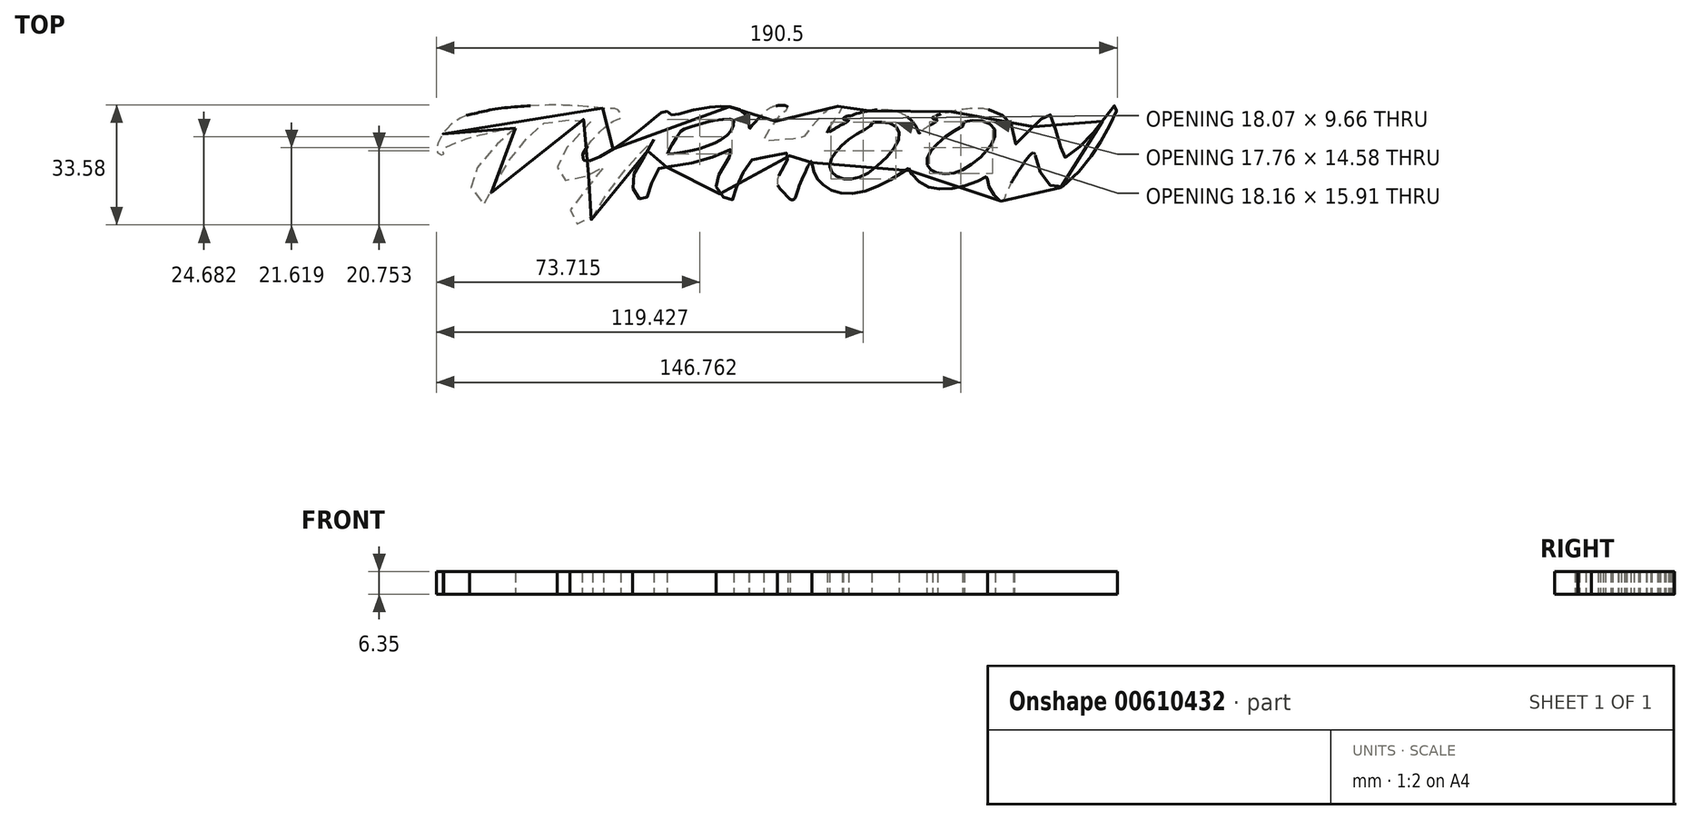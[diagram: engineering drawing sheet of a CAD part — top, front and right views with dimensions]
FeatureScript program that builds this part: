
annotation { "Feature Type Name" : "Feature", "Feature Type Description" : "" }
export const myFeature = defineFeature(function(context is Context, id is Id, definition is map)
    precondition{}
    {
        {
            var Q0;
            Q0=qCreatedBy(makeId("Top.planeOp"),FACE);
            var sketch = newSketch(context, id + "F0", { "sketchPlane" : qUnion([Q0])});
            skFitSpline(sketch, "E0", {"points": [v(22.1, 27.14) * mm, v(21.78, 26.76) * mm, v(21.16, 26.2) * mm, v(20.1, 25.33) * mm, v(18.79, 24.27) * mm, v(17.27, 22.87) * mm, v(15.75, 21.37) * mm, v(13.77, 19.23) * mm, v(12.34, 17.4) * mm, v(11.48, 16.05) * mm, v(10.24, 14.4) * mm, v(9.46, 13) * mm, v(9.33, 12.48) * mm, v(9.34, 11.55) * mm, v(9.5, 10.95) * mm, v(9.92, 10.08) * mm, v(10.5, 9) * mm, v(11.5, 7.36) * mm, v(12.18, 6.47) * mm, v(12.71, 6) * mm, v(13.12, 5.77) * mm, v(13.66, 5.75) * mm, v(14.18, 6.12) * mm, v(14.82, 7.38) * mm, v(15.18, 8.54) * mm, v(15.82, 10.13) * mm, v(16.47, 11.51) * mm, v(17.1, 12.84) * mm, v(18.08, 14.59) * mm, v(19.1, 16.22) * mm, v(20.35, 18.06) * mm, v(21.44, 19.5) * mm, v(22.74, 21.15) * mm, v(24.07, 22.8) * mm, v(25.67, 24.63) * mm, v(27.2, 26.39) * mm, v(28.29, 27.58) * mm, v(28.8, 28.03) * mm, v(29.3, 28.34) * mm, v(29.72, 28.46) * mm, v(30.82, 28.58) * mm, v(32, 28.77) * mm, v(33.32, 28.96) * mm, v(35.58, 29.2) * mm, v(37.22, 29.34) * mm, v(40.15, 29.47) * mm, v(42.2, 29.53) * mm, v(43.65, 29.52) * mm, v(43.74, 29.47) * mm, v(43.69, 29.35) * mm, v(43.37, 28.97) * mm, v(41.41, 27.03) * mm, v(39.35, 24.88) * mm, v(37.53, 22.86) * mm, v(35.8, 20.64) * mm, v(35.04, 19.48) * mm, v(34.48, 18.52) * mm, v(34.03, 17.42) * mm, v(33.9, 16.94) * mm, v(33.8, 16.2) * mm, v(33.8, 15.49) * mm, v(33.95, 14.67) * mm, v(34.14, 14.14) * mm, v(34.37, 13.75) * mm, v(34.64, 13.43) * mm, v(35.23, 12.92) * mm, v(35.95, 12.53) * mm, v(36.78, 12.28) * mm, v(37.78, 12.2) * mm, v(38.96, 12.31) * mm, v(40.2, 12.82) * mm, v(41.49, 13.43) * mm, v(42.62, 14.06) * mm, v(44.3, 15.13) * mm, v(45.26, 15.76) * mm, v(46, 16.13) * mm, v(46.39, 16.25) * mm, v(46.76, 16.25) * mm, v(46.82, 16.18) * mm, v(46.76, 15.83) * mm, v(46.5, 15.4) * mm, v(45.67, 14.52) * mm, v(44.26, 12.88) * mm, v(42.81, 11.13) * mm, v(41, 8.86) * mm, v(39.54, 6.95) * mm, v(38.25, 5.3) * mm, v(37.77, 4.7) * mm, v(37.43, 4) * mm, v(37.34, 3.46) * mm, v(37.32, 2.67) * mm, v(37.5, 2.03) * mm, v(37.99, 1.26) * mm, v(38.54, 0.73) * mm, v(39.07, 0.4) * mm, v(39.7, 0.14) * mm, v(40.72, 0) * mm, v(41.6, 0.14) * mm, v(42.26, 0.45) * mm, v(43.04, 1.13) * mm, v(43.9, 2.36) * mm, v(44.63, 3.8) * mm, v(44.88, 4.3) * mm, v(45.34, 5.08) * mm, v(46.37, 6.75) * mm, v(47.27, 8.09) * mm, v(48.44, 9.72) * mm, v(49.47, 11.1) * mm, v(50.6, 12.57) * mm, v(51.75, 14.05) * mm, v(52.9, 15.43) * mm, v(53.87, 16.58) * mm, v(54.93, 17.77) * mm, v(55.88, 18.82) * mm, v(56.76, 19.78) * mm, v(58.04, 21.16) * mm, v(59.3, 22.55) * mm, v(59.73, 23) * mm, v(60.16, 23.54) * mm, v(60.5, 23.81) * mm, v(60.76, 23.91) * mm, v(60.86, 23.9) * mm, v(60.78, 23.73) * mm, v(60.01, 22.34) * mm, v(58.95, 20.5) * mm, v(57.5, 18.13) * mm, v(56.33, 16.18) * mm, v(55.32, 14.4) * mm, v(54.92, 13.12) * mm, v(54.85, 12.4) * mm, v(54.86, 11.1) * mm, v(55.07, 10.07) * mm, v(55.33, 9.32) * mm, v(55.67, 8.64) * mm, v(56.16, 8) * mm, v(56.75, 7.4) * mm, v(57.37, 6.95) * mm, v(57.82, 6.75) * mm, v(58.22, 6.74) * mm, v(58.58, 6.97) * mm, v(58.88, 7.51) * mm, v(59.16, 8.53) * mm, v(59.41, 9.5) * mm, v(59.72, 10.49) * mm, v(60.16, 11.72) * mm, v(60.76, 13.1) * mm, v(61.6, 14.8) * mm, v(62.1, 15.63) * mm, v(62.35, 15.89) * mm, v(62.66, 16.09) * mm, v(63.03, 16.18) * mm, v(64.47, 16.19) * mm, v(65.95, 16.4) * mm, v(68.03, 16.7) * mm, v(69.76, 17.02) * mm, v(72.46, 17.58) * mm, v(74.68, 18.15) * mm, v(76.9, 18.84) * mm, v(79.27, 19.72) * mm, v(81.51, 20.76) * mm, v(82.29, 21.1) * mm, v(82.74, 21.22) * mm, v(83.1, 21.28) * mm, v(83.17, 21.2) * mm, v(82.94, 20.81) * mm, v(82.08, 19.33) * mm, v(80.96, 17.37) * mm, v(80.08, 15.75) * mm, v(78.83, 13.59) * mm, v(78.44, 12.88) * mm, v(78.25, 12.23) * mm, v(78.22, 11.54) * mm, v(78.26, 10.87) * mm, v(78.46, 10.2) * mm, v(78.76, 9.54) * mm, v(79.23, 8.84) * mm, v(79.77, 8.2) * mm, v(81.04, 7.04) * mm, v(81.75, 6.58) * mm, v(82.07, 6.5) * mm, v(82.4, 6.5) * mm, v(82.71, 6.77) * mm, v(83, 7.36) * mm, v(83.2, 8.07) * mm, v(83.4, 8.88) * mm, v(83.69, 9.9) * mm, v(84.08, 11) * mm, v(84.64, 12.32) * mm, v(85.2, 13.5) * mm, v(86.04, 15.1) * mm, v(87.16, 16.75) * mm, v(87.75, 17.74) * mm, v(88.04, 18.02) * mm, v(88.4, 18.2) * mm, v(89, 18.34) * mm, v(89.74, 18.46) * mm, v(90.75, 18.72) * mm, v(92.18, 19.03) * mm, v(95.44, 19.64) * mm, v(97.55, 20.11) * mm, v(98.16, 20.15) * mm, v(98.74, 20.08) * mm, v(98.97, 19.95) * mm, v(98.87, 19.51) * mm, v(98.57, 18.83) * mm, v(97.97, 17.87) * mm, v(96.9, 15.97) * mm, v(96.07, 14.5) * mm, v(95.62, 13.4) * mm, v(95.43, 12.73) * mm, v(95.36, 12.05) * mm, v(95.5, 11.25) * mm, v(95.79, 10.55) * mm, v(96.52, 9.69) * mm, v(97.5, 8.7) * mm, v(98.2, 7.85) * mm, v(98.67, 7.4) * mm, v(99.23, 7.08) * mm, v(99.61, 7.02) * mm, v(100, 7.14) * mm, v(100.34, 7.53) * mm, v(100.72, 8.46) * mm, v(101.1, 9.74) * mm, v(101.68, 11.3) * mm, v(102.35, 12.93) * mm, v(103.19, 14.75) * mm, v(103.98, 16.45) * mm, v(104.3, 17.07) * mm, v(104.6, 17.48) * mm, v(104.81, 17.71) * mm, v(104.97, 17.84) * mm, v(105.04, 17.82) * mm, v(105.05, 17.53) * mm, v(105.15, 16.62) * mm, v(105.53, 15.18) * mm, v(105.82, 14.36) * mm, v(106.42, 13.06) * mm, v(106.57, 12.8) * mm, v(107.08, 12.24) * mm, v(107.99, 11.36) * mm, v(109.14, 10.47) * mm, v(110.32, 9.8) * mm, v(111.68, 9.24) * mm, v(112.92, 8.95) * mm, v(114.8, 8.78) * mm, v(116.77, 8.86) * mm, v(119.17, 9.24) * mm, v(121.73, 10.03) * mm, v(124.2, 11.09) * mm, v(126.82, 12.47) * mm, v(129.65, 14.22) * mm, v(130.15, 14.62) * mm, v(131.6, 15.56) * mm, v(132, 15.75) * mm, v(132.12, 15.78) * mm, v(132.2, 15.68) * mm, v(132.5, 15.1) * mm, v(133.14, 14.06) * mm, v(134.2, 12.8) * mm, v(135.2, 11.96) * mm, v(136.82, 11.02) * mm, v(138.5, 10.37) * mm, v(140.07, 10.06) * mm, v(142.32, 10) * mm, v(144.8, 10.22) * mm, v(146.99, 10.71) * mm, v(149.9, 11.72) * mm, v(151.73, 12.42) * mm, v(153.05, 13.12) * mm, v(153.89, 13.48) * mm, v(154.26, 13.6) * mm, v(154.35, 13.54) * mm, v(154.24, 12.93) * mm, v(154.2, 12.4) * mm, v(154.24, 11.87) * mm, v(154.47, 11.1) * mm, v(154.97, 10.04) * mm, v(155.75, 8.78) * mm, v(156.44, 7.7) * mm, v(157.27, 6.88) * mm, v(157.85, 6.67) * mm, v(158.25, 6.68) * mm, v(158.65, 7.02) * mm, v(159.19, 8.03) * mm, v(159.52, 9.03) * mm, v(160.03, 10.18) * mm, v(160.47, 11.03) * mm, v(161.17, 12.38) * mm, v(161.87, 13.5) * mm, v(163.1, 15.44) * mm, v(164.32, 17.22) * mm, v(164.88, 18.08) * mm, v(165.63, 18.97) * mm, v(166.16, 19.64) * mm, v(166.58, 20.02) * mm, v(166.9, 20.15) * mm, v(167.17, 20.1) * mm, v(167.37, 19.85) * mm, v(167.86, 18.69) * mm, v(168.36, 16.92) * mm, v(168.78, 15.2) * mm, v(169.44, 13.56) * mm, v(170.24, 12.37) * mm, v(171.66, 11.14) * mm, v(173.03, 10.47) * mm, v(173.86, 10.3) * mm, v(174.63, 10.43) * mm, v(175.35, 10.88) * mm, v(177.63, 12.83) * mm, v(179.75, 14.97) * mm, v(181.34, 16.8) * mm, v(182.68, 18.59) * mm, v(183.8, 20.19) * mm, v(184.72, 21.53) * mm, v(185.74, 23.12) * mm, v(186.71, 24.72) * mm, v(187.68, 26.5) * mm, v(188.59, 28.25) * mm, v(189.24, 29.62) * mm, v(189.9, 31.03) * mm, v(190.32, 32.05) * mm, v(190.44, 32.64) * mm, v(190.5, 33.05) * mm, v(190.43, 33.49) * mm, v(190.22, 33.58) * mm, v(189.81, 33.43) * mm, v(189.22, 32.7) * mm, v(188.1, 31.32) * mm, v(187.13, 30.05) * mm, v(186.02, 28.6) * mm, v(184.75, 27.02) * mm, v(183.59, 25.6) * mm, v(182.02, 23.86) * mm, v(180.59, 22.43) * mm, v(178.96, 20.94) * mm, v(177.1, 19.5) * mm, v(175.85, 18.82) * mm, v(175.43, 18.67) * mm, v(175.35, 18.68) * mm, v(175.17, 19.46) * mm, v(174.8, 20.97) * mm, v(174.33, 22.85) * mm, v(173.8, 24.71) * mm, v(173.26, 26.6) * mm, v(172.73, 28.32) * mm, v(172.16, 30.02) * mm, v(171.8, 30.72) * mm, v(171.5, 31.03) * mm, v(171.23, 31.12) * mm, v(170.92, 31.05) * mm, v(170.38, 30.69) * mm, v(169.08, 29.54) * mm, v(167.4, 27.94) * mm, v(166.02, 26.56) * mm, v(164.7, 25.25) * mm, v(163.29, 23.83) * mm, v(162.26, 22.75) * mm, v(162.03, 22.52) * mm, v(161.75, 22.32) * mm, v(161.5, 22.25) * mm, v(161.44, 22.29) * mm, v(161.48, 22.42) * mm, v(161.66, 23.52) * mm, v(161.7, 25.32) * mm, v(161.46, 26.6) * mm, v(161.2, 27.39) * mm, v(160.82, 28.2) * mm, v(160.37, 28.85) * mm, v(160.34, 28.9) * mm, v(159.5, 29.81) * mm, v(158.6, 30.53) * mm, v(157.65, 31.12) * mm, v(156.57, 31.65) * mm, v(155.3, 32.04) * mm, v(153.61, 32.42) * mm, v(152, 32.57) * mm, v(149.9, 32.57) * mm, v(147.57, 32.35) * mm, v(144.9, 31.89) * mm, v(142.31, 31.24) * mm, v(139.64, 30.57) * mm, v(138.9, 30.15) * mm, v(138.81, 29.91) * mm, v(138.92, 29.72) * mm, v(139.58, 29.51) * mm, v(140.05, 29.42) * mm, v(140.22, 29.3) * mm, v(140.14, 29.13) * mm, v(137.97, 27.78) * mm, v(136.3, 26.7) * mm, v(135.84, 26.3) * mm, v(135.49, 25.96) * mm, v(135.1, 25.76) * mm, v(134.95, 25.71) * mm, v(134.87, 25.82) * mm, v(134.6, 26.63) * mm, v(134.13, 27.58) * mm, v(133.68, 28.29) * mm, v(133.4, 28.61) * mm, v(132.7, 29.4) * mm, v(131.6, 30.3) * mm, v(130.55, 30.93) * mm, v(128.6, 31.7) * mm, v(126.87, 32.07) * mm, v(124.97, 32.2) * mm, v(123.46, 32.19) * mm, v(121.7, 32) * mm, v(119.36, 31.59) * mm, v(117.03, 30.94) * mm, v(115.98, 30.53) * mm, v(115.56, 30.48) * mm, v(114.84, 30.4) * mm, v(114.51, 30.31) * mm, v(114.3, 30.26) * mm, v(114, 30) * mm, v(113.86, 29.78) * mm, v(113.86, 29.59) * mm, v(114.12, 29.46) * mm, v(114.72, 29.39) * mm, v(115.28, 29.37) * mm, v(115.35, 29.28) * mm, v(115.28, 29.17) * mm, v(114.28, 28.46) * mm, v(112.79, 27.73) * mm, v(112, 27.24) * mm, v(110.95, 26.57) * mm, v(110.24, 26.16) * mm, v(109.7, 25.92) * mm, v(109.48, 25.85) * mm, v(109.4, 25.85) * mm, v(109.4, 25.94) * mm, v(109.7, 26.68) * mm, v(110.21, 27.56) * mm, v(110.98, 28.72) * mm, v(111.67, 29.78) * mm, v(112.76, 31.4) * mm, v(113.34, 32.59) * mm, v(113.53, 33.16) * mm, v(113.53, 33.2) * mm, v(113.36, 33.2) * mm, v(111.95, 33.18) * mm, v(110.96, 33.03) * mm, v(110.18, 32.8) * mm, v(109.6, 32.48) * mm, v(109.16, 32.06) * mm, v(108.7, 31.54) * mm, v(108.05, 30.8) * mm, v(107.56, 30.28) * mm, v(106.96, 29.63) * mm, v(106.2, 28.78) * mm, v(105.38, 27.86) * mm, v(104.36, 26.64) * mm, v(103.62, 25.68) * mm, v(103.1, 25) * mm, v(102.77, 24.7) * mm, v(102.31, 24.44) * mm, v(101.5, 24.23) * mm, v(100.03, 24.05) * mm, v(97.8, 23.99) * mm, v(95.08, 23.75) * mm, v(93.14, 23.55) * mm, v(91.77, 23.54) * mm, v(91.57, 23.58) * mm, v(91.56, 23.66) * mm, v(92.38, 25.37) * mm, v(93.63, 27.34) * mm, v(95.55, 29.8) * mm, v(97.03, 31.59) * mm, v(97.52, 31.88) * mm, v(98, 32.18) * mm, v(98.25, 32.46) * mm, v(98.28, 32.9) * mm, v(98.1, 33.16) * mm, v(97.62, 33.37) * mm, v(96.5, 33.45) * mm, v(95.58, 33.4) * mm, v(94.75, 33.24) * mm, v(94.03, 32.99) * mm, v(93.04, 32.48) * mm, v(91.77, 31.5) * mm, v(90.23, 29.91) * mm, v(88.86, 28.38) * mm, v(88.31, 27.76) * mm, v(88.07, 27.5) * mm, v(87.9, 27.19) * mm, v(87.72, 27) * mm, v(87.52, 26.92) * mm, v(87.43, 26.91) * mm, v(87.44, 27.1) * mm, v(87.43, 28.5) * mm, v(87.17, 29.6) * mm, v(86.64, 30.69) * mm, v(86.1, 31.36) * mm, v(84.96, 32.19) * mm, v(83.74, 32.69) * mm, v(82.03, 33.07) * mm, v(80.58, 33.18) * mm, v(79.37, 33.19) * mm, v(78.11, 33.13) * mm, v(74.28, 32.64) * mm, v(70.35, 31.81) * mm, v(67.6, 30.98) * mm, v(66.72, 30.77) * mm, v(65.96, 30.76) * mm, v(65.46, 31) * mm, v(65.1, 31.3) * mm, v(64.65, 31.69) * mm, v(64.3, 31.83) * mm, v(63.84, 31.83) * mm, v(63.16, 31.55) * mm, v(62.13, 30.79) * mm, v(61.17, 29.97) * mm, v(59.7, 28.8) * mm, v(58.42, 27.76) * mm, v(56.6, 26.3) * mm, v(55.37, 25.34) * mm, v(53.06, 23.62) * mm, v(50.4, 21.81) * mm, v(46.44, 19.48) * mm, v(44.31, 18.42) * mm, v(43, 17.99) * mm, v(42, 17.83) * mm, v(41.54, 17.89) * mm, v(41.2, 18.12) * mm, v(40.9, 18.58) * mm, v(40.8, 19.01) * mm, v(41.04, 20.04) * mm, v(41.64, 21.14) * mm, v(42.78, 22.76) * mm, v(44.33, 24.6) * mm, v(45.93, 26.22) * mm, v(47.46, 27.61) * mm, v(48.97, 28.67) * mm, v(50.16, 29.3) * mm, v(50.95, 29.55) * mm, v(51.33, 29.75) * mm, v(51.49, 29.92) * mm, v(51.56, 30.42) * mm, v(51.36, 31.37) * mm, v(51.1, 31.92) * mm, v(50.78, 32.2) * mm, v(50.16, 32.45) * mm, v(48.11, 32.5) * mm, v(45, 32.82) * mm, v(41.82, 33.13) * mm, v(37.38, 33.4) * mm, v(34.67, 33.51) * mm, v(31.56, 33.5) * mm, v(26.44, 33.34) * mm, v(20.88, 32.93) * mm, v(15.6, 32.26) * mm, v(11.93, 31.47) * mm, v(9.09, 30.8) * mm, v(7.61, 30.28) * mm, v(6.32, 29.65) * mm, v(5.48, 29.14) * mm, v(4.65, 28.54) * mm, v(3.77, 27.77) * mm, v(3.02, 26.98) * mm, v(2.18, 25.94) * mm, v(1.55, 24.98) * mm, v(1, 23.94) * mm, v(0.48, 22.87) * mm, v(0.12, 21.92) * mm, v(0, 21.28) * mm, v(0.11, 20.58) * mm, v(0.56, 19.94) * mm, v(1.26, 19.56) * mm, v(1.83, 19.52) * mm, v(2.02, 19.63) * mm, v(2.07, 19.94) * mm, v(1.99, 20.4) * mm, v(1.9, 20.7) * mm, v(1.96, 21.02) * mm, v(2.19, 21.36) * mm, v(2.73, 21.8) * mm, v(4.25, 22.5) * mm, v(5.24, 22.92) * mm, v(7.8, 23.86) * mm, v(9.82, 24.51) * mm, v(11.85, 25.08) * mm, v(13.12, 25.37) * mm, v(15.82, 26.02) * mm, v(18.38, 26.57) * mm, v(20.5, 27.03) * mm, v(21.69, 27.18) * mm, v(22.06, 27.18) * mm, v(22.1, 27.14) * mm]});
            skFitSpline(sketch, "E1", {"points": [v(64.68, 19.85) * mm, v(64.6, 19.87) * mm, v(64.69, 20.12) * mm, v(65.07, 20.99) * mm, v(65.5, 21.85) * mm, v(66.26, 23.11) * mm, v(67.16, 24.45) * mm, v(68.3, 26.03) * mm, v(68.73, 26.62) * mm, v(69.03, 26.74) * mm, v(70.06, 27.1) * mm, v(71.42, 27.54) * mm, v(73.23, 28.08) * mm, v(74.83, 28.53) * mm, v(76.68, 28.98) * mm, v(78.4, 29.29) * mm, v(80.35, 29.54) * mm, v(81.7, 29.64) * mm, v(82.6, 29.56) * mm, v(82.94, 29.43) * mm, v(83.17, 29.25) * mm, v(83.23, 28.83) * mm, v(83.13, 27.88) * mm, v(82.84, 26.92) * mm, v(82.33, 26.12) * mm, v(81.56, 25.3) * mm, v(80.38, 24.43) * mm, v(78.94, 23.51) * mm, v(78.04, 23.02) * mm, v(76.77, 22.42) * mm, v(75.02, 21.75) * mm, v(73.54, 21.3) * mm, v(71.89, 20.86) * mm, v(69.24, 20.35) * mm, v(67.14, 20.06) * mm, v(65.16, 19.9) * mm, v(64.68, 19.85) * mm]});
            skFitSpline(sketch, "E2", {"points": [v(122.03, 28.7) * mm, v(123.41, 28.77) * mm, v(125.33, 28.73) * mm, v(126.55, 28.55) * mm, v(127.68, 28.17) * mm, v(128.6, 27.53) * mm, v(129.17, 26.77) * mm, v(129.45, 25.88) * mm, v(129.45, 24.85) * mm, v(129.2, 23.63) * mm, v(128.59, 22.28) * mm, v(127.06, 20.15) * mm, v(125, 18.04) * mm, v(122.32, 15.7) * mm, v(120.37, 14.33) * mm, v(118.7, 13.5) * mm, v(117.59, 13.12) * mm, v(116.04, 12.87) * mm, v(115.31, 12.8) * mm, v(113.72, 13) * mm, v(112.25, 13.48) * mm, v(111.64, 13.83) * mm, v(111.02, 14.3) * mm, v(110.61, 14.8) * mm, v(110.2, 15.66) * mm, v(110.06, 16.56) * mm, v(110.2, 17.72) * mm, v(110.65, 18.85) * mm, v(111.18, 19.65) * mm, v(111.97, 20.6) * mm, v(113.2, 21.96) * mm, v(114.52, 23.24) * mm, v(116.17, 24.55) * mm, v(117.76, 25.6) * mm, v(119.29, 26.49) * mm, v(120.87, 27.23) * mm, v(121.37, 27.6) * mm, v(121.62, 27.9) * mm, v(121.85, 28.5) * mm, v(121.86, 28.65) * mm, v(122.03, 28.7) * mm]});
            skFitSpline(sketch, "E3", {"points": [v(147.67, 28.9) * mm, v(149.2, 29.2) * mm, v(151.5, 29.23) * mm, v(153.27, 28.94) * mm, v(154.88, 28.26) * mm, v(155.83, 27.34) * mm, v(156.35, 26.02) * mm, v(156.32, 25) * mm, v(155.83, 23.53) * mm, v(154.99, 22.14) * mm, v(154.03, 20.89) * mm, v(152.91, 19.64) * mm, v(150.4, 17.46) * mm, v(147.92, 15.76) * mm, v(146.24, 14.96) * mm, v(144.21, 14.44) * mm, v(142.27, 14.25) * mm, v(140.13, 14.54) * mm, v(139.2, 14.88) * mm, v(138.43, 15.31) * mm, v(137.86, 15.86) * mm, v(137.32, 16.77) * mm, v(137.15, 17.58) * mm, v(137.32, 18.81) * mm, v(138.15, 20.43) * mm, v(139.22, 21.83) * mm, v(141.17, 23.72) * mm, v(143.5, 25.4) * mm, v(145.85, 26.8) * mm, v(147.47, 27.74) * mm, v(147.6, 27.82) * mm, v(147.66, 27.88) * mm, v(147.56, 28.08) * mm, v(147.32, 28.28) * mm, v(147.2, 28.6) * mm, v(147.39, 28.83) * mm, v(147.67, 28.9) * mm]});
            skSolve(sketch);
        }
        {
            var Q0;
            Q0 = qSketchRegion(id + "F0", true);
            extrude(context, id + "F1", {"entities" : qUnion([Q0]), "depth" : 6.35 * mm, "offsetDistance" : 25.4 * mm});
        }
    });
